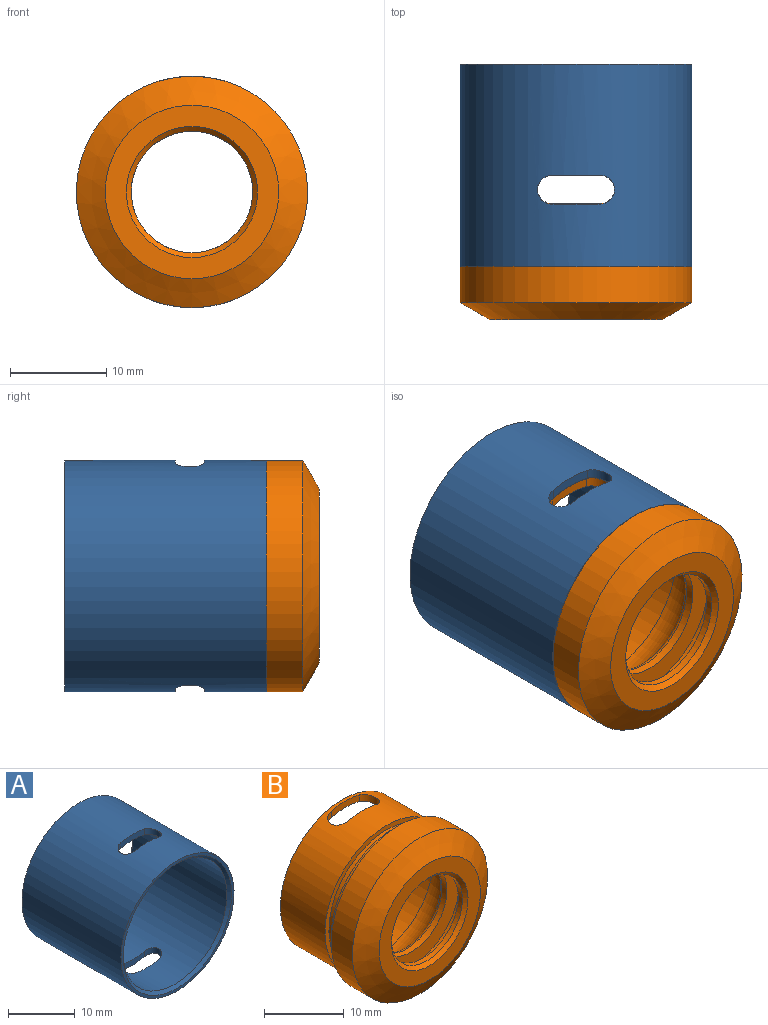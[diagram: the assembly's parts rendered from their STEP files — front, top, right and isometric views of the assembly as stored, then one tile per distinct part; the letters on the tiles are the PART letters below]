
ASSEMBLY  parts=2 mates=1
PART A: 14 faces, bbox 24x21x24 mm
  f0: cylinder r=11mm len=22mm, axis (0,1,0), area 1337.3mm2, adj f4,f5,f6,f7,f8,f9,f10,f11
  f1: cylinder r=12mm len=24mm, axis (0,1,0), area 1538.5mm2, adj f2,f3,f4,f5,f6,f7,f8,f9
  f2: plane 24x24mm, normal (0,-1,0), area 36.9mm2, adj f1,f13
  f3: plane 24x24mm, normal (0,1,0), area 36.9mm2, adj f1,f12
  f4: cylinder r=1.5mm len=3mm, axis (0,0,-1), area 4.9mm2, adj f0,f1,f5,f7
  f5: plane 5x1.29mm, normal (0,1,0), area 5mm2, adj f0,f1,f4,f6
  f6: cylinder r=1.5mm len=3mm, axis (0,0,-1), area 4.9mm2, adj f0,f1,f5,f7
  f7: plane 5x1.29mm, normal (0,-1,0), area 5mm2, adj f0,f1,f4,f6
  f8: plane 5x1.29mm, normal (0,-1,0), area 5mm2, adj f0,f1,f9,f11
  f9: cylinder r=1.5mm len=3mm, axis (0,0,-1), area 4.9mm2, adj f0,f1,f8,f10
  f10: plane 5x1.29mm, normal (0,1,0), area 5mm2, adj f0,f1,f9,f11
  f11: cylinder r=1.5mm len=3mm, axis (0,0,-1), area 4.9mm2, adj f0,f1,f8,f10
  f12: cone r=11.5mm half-angle=45deg, axis (0,1,0), area 50mm2, adj f0,f3
  f13: cone r=11mm half-angle=45deg, axis (0,-1,0), area 50mm2, adj f0,f2
PART B: 28 faces, bbox 24x15.5x24 mm
  f0: cylinder r=6.3mm len=12.6mm, axis (0,-1,0), area 34.9mm2, adj f21,f25
  f1: cylinder r=11mm len=22mm, axis (0,1,0), area 69.1mm2, adj f15,f23
  f2: cylinder r=10mm len=20mm, axis (0,1,0), area 323.7mm2, adj f5,f6,f7,f8,f9,f10,f11,f12
  f3: cylinder r=11mm len=22mm, axis (0,1,0), area 501mm2, adj f4,f5,f6,f7,f8,f9,f10,f11
  f4: plane 22x22mm, normal (0,1,0), area 46.8mm2, adj f3,f18
  f5: cylinder r=1.5mm len=3mm, axis (0,0,-1), area 5mm2, adj f2,f3,f6,f8
  f6: plane 5x1.32mm, normal (0,1,0), area 5mm2, adj f2,f3,f5,f7
  f7: cylinder r=1.5mm len=3mm, axis (0,0,-1), area 5mm2, adj f2,f3,f6,f8
  f8: plane 5x1.32mm, normal (0,-1,0), area 5mm2, adj f2,f3,f5,f7
  f9: plane 5x1.32mm, normal (0,-1,0), area 5mm2, adj f2,f3,f10,f12
  f10: cylinder r=1.5mm len=3mm, axis (0,0,-1), area 5mm2, adj f2,f3,f9,f11
  f11: plane 5x1.32mm, normal (0,1,0), area 5mm2, adj f2,f3,f10,f12
  f12: cylinder r=1.5mm len=3mm, axis (0,0,-1), area 5mm2, adj f2,f3,f9,f11
  f13: cylinder r=12mm len=24mm, axis (0,1,0), area 284.1mm2, adj f15,f20
  f14: plane 18x18mm, normal (0,-1,0), area 109.2mm2, adj f19,f20
  f15: plane 24x24mm, normal (0,1,0), area 72.3mm2, adj f1,f13
  f16: cylinder r=6.3mm len=12.6mm, axis (0,-1,0), area 29.7mm2, adj f19,f26
  f17: torus R=5mm, axis (0,-1,0), area 342.8mm2, adj f2,f21
  f18: cone r=10.3mm half-angle=45deg, axis (0,1,0), area 27.1mm2, adj f2,f4
  f19: cone r=6.3mm half-angle=45deg, axis (0,-1,0), area 29.1mm2, adj f14,f16
  f20: cone r=9mm half-angle=60deg, axis (0,1,0), area 228.5mm2, adj f13,f14
  f21: torus R=6.8mm, axis (0,1,0), area 24.9mm2, adj f0,f17
  f22: plane 22x22mm, normal (0,-1,0), area 46.8mm2, adj f3,f24
  f23: plane 22x22mm, normal (0,1,0), area 46.8mm2, adj f1,f24
  f24: cylinder r=10.3mm len=20.6mm, axis (0,-1,0), area 71.2mm2, adj f22,f23
  f25: plane 17x17mm, normal (0,-1,0), area 102.3mm2, adj f0,f27
  f26: plane 17x17mm, normal (0,1,0), area 102.3mm2, adj f16,f27
  f27: cylinder r=8.5mm len=17mm, axis (0,-1,0), area 106.8mm2, adj f25,f26
PLACE A t=(-16.53,-6.49,0.19)mm
PLACE B t=(-16.53,-17.45,0.19)mm
MATE slider B.f13 <-> A.f1  axis (0,1,0) through (-16.53,-27.45,0.19)mm
